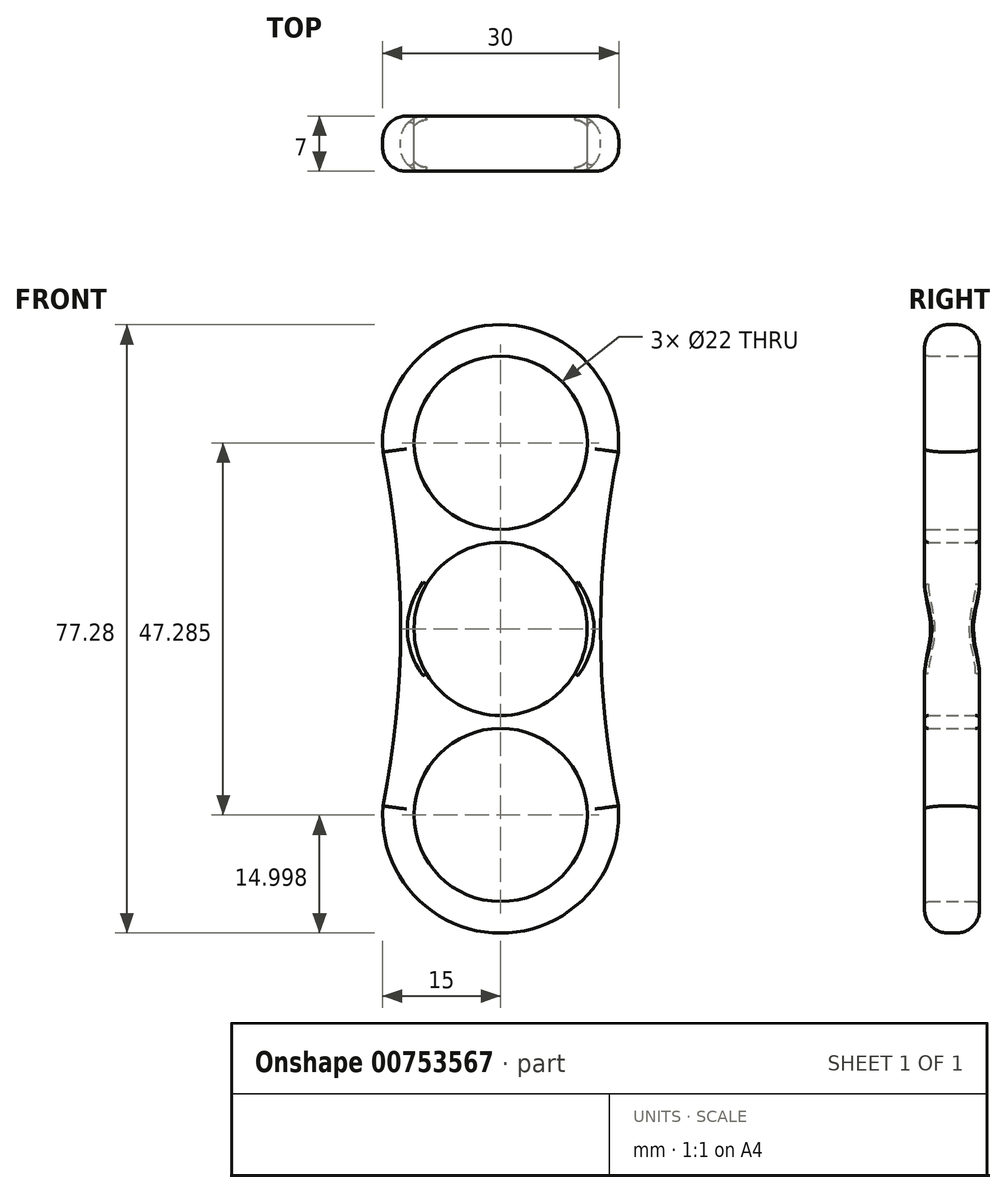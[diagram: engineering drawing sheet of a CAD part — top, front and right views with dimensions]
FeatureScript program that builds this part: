
annotation { "Feature Type Name" : "Feature", "Feature Type Description" : "" }
export const myFeature = defineFeature(function(context is Context, id is Id, definition is map)
    precondition{}
    {
        {
            var Q0;
            Q0=qCreatedBy(makeId("Front.planeOp"),FACE);
            var sketch = newSketch(context, id + "F0", { "sketchPlane" : qUnion([Q0])});
            skCircle(sketch, "E0", {"center": v(0, 23.64) * mm, "radius": 15 * mm});
            skCircle(sketch, "E1.1.0", {"center": v(0, -23.64) * mm, "radius": 15 * mm});
            skPoint(sketch, "E1.center", {"position": v(0, 0) * mm});
            skLineSegment(sketch, "E2", {"start": v(-33.25, 23.64) * mm, "end": v(43.64, 23.64) * mm, "construction": true});
            skLineSegment(sketch, "E3", {"start": v(43.64, 23.64) * mm, "end": v(43.64, -23.64) * mm, "construction": true});
            skLineSegment(sketch, "E4", {"start": v(43.64, -23.64) * mm, "end": v(-33.25, -23.64) * mm, "construction": true});
            skLineSegment(sketch, "E5", {"start": v(-33.25, -23.64) * mm, "end": v(-33.25, 23.64) * mm, "construction": true});
            skCircle(sketch, "E6", {"center": v(0, 0) * mm, "radius": 11 * mm});
            skArc(sketch, "E7", {"start": v(-14.96, -22.48) * mm, "mid": v(-12.7, 0) * mm, "end": v(-14.95, 22.46) * mm});
            skArc(sketch, "E8.MirrorCS", {"start": v(14.96, -22.48) * mm, "mid": v(12.7, 0) * mm, "end": v(14.95, 22.46) * mm});
            skCircle(sketch, "E9", {"center": v(0, 23.64) * mm, "radius": 11 * mm});
            skCircle(sketch, "E10", {"center": v(0, -23.64) * mm, "radius": 11 * mm});
            skSolve(sketch);
        }
        {
            var Q0;
            Q0=makeQuery(id+"F0.imprint","IMPRINT",FACE,{"disambiguationData":[TD([[makeQuery(id+"F0.imprint","IMPRINT",EDGE,{"derivedFrom":sQuery(id+"F0.wireOp",EDGE,"E9")}),-1.0]])]});
            var Q1;
            {var subQ0=sQuery(id+"F0.wireOp",EDGE,"E7");var subQ1=sQuery(id+"F0.wireOp",EDGE,"E0");var subQ2=makeQuery(id+"F0.imprint","INTERSECT",VERTEX,{"disambiguationData":[OD(1.0)],"derivedFrom":[subQ1,subQ0]});Q1=makeQuery(id+"F0.imprint","IMPRINT",FACE,{"disambiguationData":[TD([[makeQuery(id+"F0.imprint","IMPRINT",EDGE,{"disambiguationData":[TD([[subQ2,-1.0]])],"derivedFrom":subQ1}),-1.0]])]});}
            var Q2;
            {var subQ0=sQuery(id+"F0.wireOp",EDGE,"E8.MirrorCS");var subQ1=sQuery(id+"F0.wireOp",EDGE,"E0");var subQ2=makeQuery(id+"F0.imprint","INTERSECT",VERTEX,{"disambiguationData":[OD(1.0)],"derivedFrom":[subQ1,subQ0]});Q2=makeQuery(id+"F0.imprint","IMPRINT",FACE,{"disambiguationData":[TD([[makeQuery(id+"F0.imprint","IMPRINT",EDGE,{"disambiguationData":[TD([[subQ2,1.0]])],"derivedFrom":subQ1}),-1.0]])]});}
            var Q3;
            Q3=makeQuery(id+"F0.imprint","IMPRINT",FACE,{"disambiguationData":[TD([[makeQuery(id+"F0.imprint","IMPRINT",EDGE,{"derivedFrom":sQuery(id+"F0.wireOp",EDGE,"E10")}),-1.0]])]});
            extrude(context, id + "F1", {"entities" : qUnion([Q0, Q1, Q2, Q3]), "depth" : 7 * mm, "offsetDistance" : 25.4 * mm});
        }
        {
            var Q0;
            Q0=makeQuery(id+"F1.opExtrude","CAP_EDGE",EDGE,{"disambiguationData":[OSD([sQuery(id+"F0.wireOp",EDGE,"E7")])],"isStart":false});
            var Q1;
            Q1=makeQuery(id+"F1.opExtrude","CAP_EDGE",EDGE,{"disambiguationData":[OSD([sQuery(id+"F0.wireOp",EDGE,"E0")])],"isStart":false});
            var Q2;
            Q2=makeQuery(id+"F1.opExtrude","CAP_EDGE",EDGE,{"disambiguationData":[OSD([sQuery(id+"F0.wireOp",EDGE,"E8.MirrorCS")])],"isStart":false});
            var Q3;
            Q3=makeQuery(id+"F1.opExtrude","CAP_EDGE",EDGE,{"disambiguationData":[OSD([sQuery(id+"F0.wireOp",EDGE,"E1.1.0")])],"isStart":false});
            var Q4;
            Q4=makeQuery(id+"F1.opExtrude","CAP_EDGE",EDGE,{"disambiguationData":[OSD([sQuery(id+"F0.wireOp",EDGE,"E7")])],"isStart":true});
            var Q5;
            Q5=makeQuery(id+"F1.opExtrude","CAP_EDGE",EDGE,{"disambiguationData":[OSD([sQuery(id+"F0.wireOp",EDGE,"E0")])],"isStart":true});
            var Q6;
            Q6=makeQuery(id+"F1.opExtrude","CAP_EDGE",EDGE,{"disambiguationData":[OSD([sQuery(id+"F0.wireOp",EDGE,"E8.MirrorCS")])],"isStart":true});
            var Q7;
            Q7=makeQuery(id+"F1.opExtrude","CAP_EDGE",EDGE,{"disambiguationData":[OSD([sQuery(id+"F0.wireOp",EDGE,"E1.1.0")])],"isStart":true});
            fillet(context, id + "F2", {"entities" : qUnion([Q0, Q1, Q2, Q3, Q4, Q5, Q6, Q7]), "radius" : 3 * mm, "tangentPropagation" : true, "allowEdgeOverflow" : false});
        }
        {
            var Q0;
            Q0=makeQuery(id+"F1.opExtrude","CAP_EDGE",EDGE,{"disambiguationData":[OSD([sQuery(id+"F0.wireOp",EDGE,"E9")])],"isStart":true});
            var Q1;
            Q1=makeQuery(id+"F1.opExtrude","CAP_EDGE",EDGE,{"disambiguationData":[OSD([sQuery(id+"F0.wireOp",EDGE,"E6")])],"isStart":true});
            var Q2;
            Q2=makeQuery(id+"F1.opExtrude","CAP_EDGE",EDGE,{"disambiguationData":[OSD([sQuery(id+"F0.wireOp",EDGE,"E10")])],"isStart":true});
            var Q3;
            Q3=makeQuery(id+"F1.opExtrude","CAP_EDGE",EDGE,{"disambiguationData":[OSD([sQuery(id+"F0.wireOp",EDGE,"E6")])],"isStart":false});
            var Q4;
            Q4=makeQuery(id+"F1.opExtrude","CAP_EDGE",EDGE,{"disambiguationData":[OSD([sQuery(id+"F0.wireOp",EDGE,"E9")])],"isStart":false});
            var Q5;
            Q5=makeQuery(id+"F1.opExtrude","CAP_EDGE",EDGE,{"disambiguationData":[OSD([sQuery(id+"F0.wireOp",EDGE,"E10")])],"isStart":false});
            fillet(context, id + "F3", {"entities" : qUnion([Q0, Q1, Q2, Q3, Q4, Q5]), "radius" : .5 * mm, "tangentPropagation" : true, "allowEdgeOverflow" : false});
        }
    });
